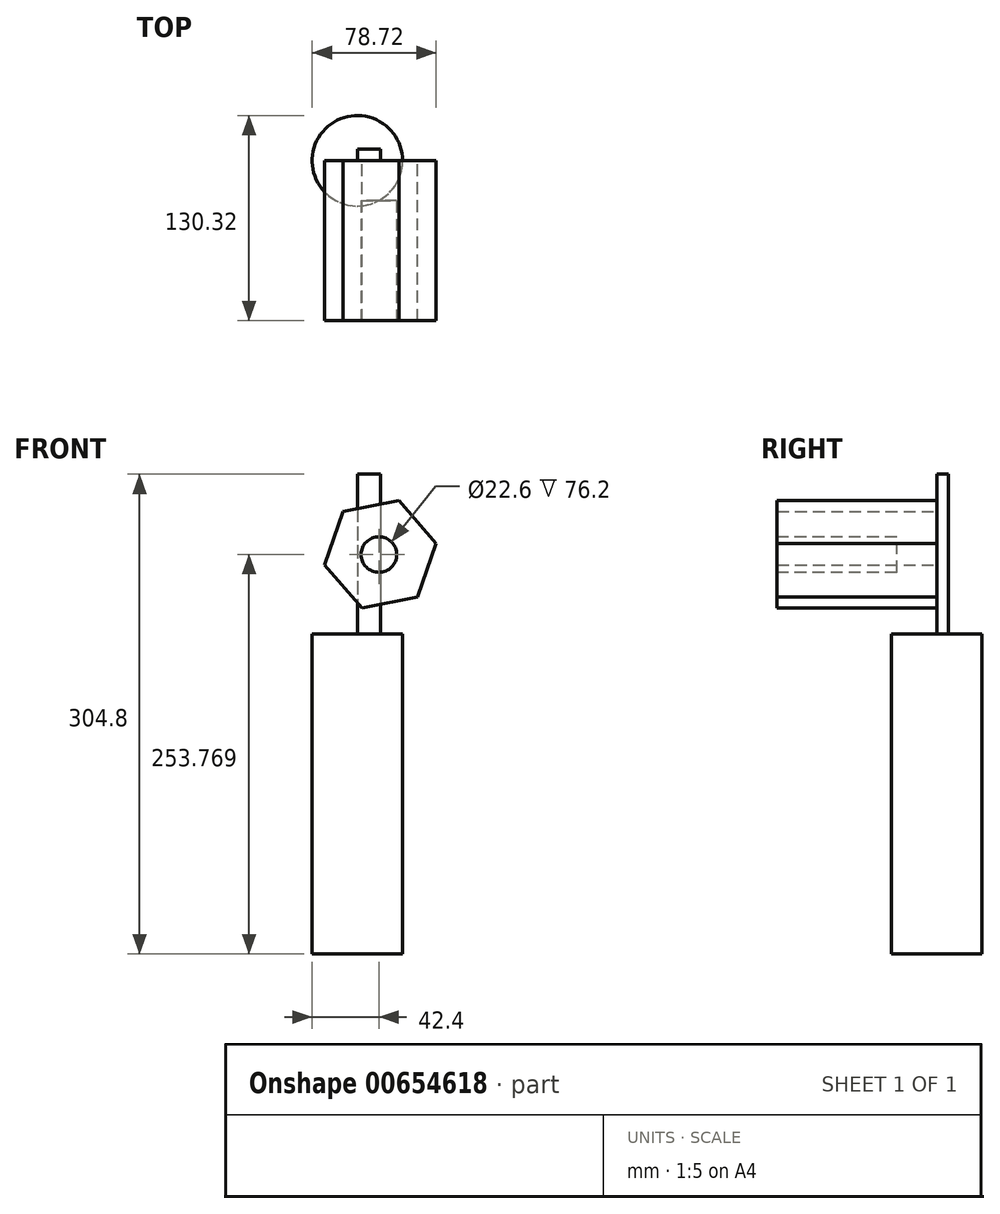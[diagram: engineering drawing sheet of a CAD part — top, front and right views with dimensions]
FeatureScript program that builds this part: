
annotation { "Feature Type Name" : "Feature", "Feature Type Description" : "" }
export const myFeature = defineFeature(function(context is Context, id is Id, definition is map)
    precondition{}
    {
        {
            var Q0;
            Q0=qCreatedBy(makeId("Top.planeOp"),FACE);
            var sketch = newSketch(context, id + "F0", { "sketchPlane" : qUnion([Q0])});
            skCircle(sketch, "E0", {"center": v(0, 0) * mm, "radius": 28.72 * mm});
            skSolve(sketch);
        }
        {
            var Q0;
            Q0 = qSketchRegion(id + "F0", true);
            extrude(context, id + "F1", {"entities" : qUnion([Q0]), "depth" : 203.2 * mm, "offsetDistance" : 25.4 * mm});
        }
        {
            var Q0;
            Q0=makeQuery(id+"F1.opExtrude","CAP_FACE",FACE,{"disambiguationData":[OSD([sQuery(id+"F0.wireOp",EDGE,"E0")])],"isStart":false});
            var sketch = newSketch(context, id + "F2", { "sketchPlane" : qUnion([Q0])});
            skLineSegment(sketch, "E1.bottom", {"start": v(0, 0) * mm, "end": v(14.6, 0) * mm});
            skLineSegment(sketch, "E1.top", {"start": v(0, 7.47) * mm, "end": v(14.6, 7.47) * mm});
            skLineSegment(sketch, "E1.left", {"start": v(0, 0) * mm, "end": v(0, 7.47) * mm});
            skLineSegment(sketch, "E1.right", {"start": v(14.6, 0) * mm, "end": v(14.6, 7.47) * mm});
            skSolve(sketch);
        }
        {
            var Q0;
            Q0 = qSketchRegion(id + "F2", true);
            extrude(context, id + "F3", {"entities" : qUnion([Q0]), "operationType" : NewBodyOperationType.ADD, "depth" : 101.6 * mm, "offsetDistance" : 25.4 * mm});
        }
        {
            var Q0;
            Q0=makeQuery(id+"F3.opExtrude","SWEPT_FACE",FACE,{"disambiguationData":[OSD([sQuery(id+"F2.wireOp",EDGE,"E1.bottom")])]});
            var sketch = newSketch(context, id + "F4", { "sketchPlane" : qUnion([Q0])});
            skCircle(sketch, "E2.cCircle", {"center": v(14.6, 254) * mm, "radius": 31.24 * mm, "construction": true});
            skLineSegment(sketch, "E2.0", {"start": v(50, 260.9) * mm, "end": v(38.27, 226.79) * mm});
            skLineSegment(sketch, "E2.1", {"start": v(38.27, 226.79) * mm, "end": v(2.86, 219.89) * mm});
            skLineSegment(sketch, "E2.2", {"start": v(2.86, 219.89) * mm, "end": v(-20.82, 247.1) * mm});
            skLineSegment(sketch, "E2.3", {"start": v(-20.82, 247.1) * mm, "end": v(-9.09, 281.21) * mm});
            skLineSegment(sketch, "E2.4", {"start": v(-9.09, 281.21) * mm, "end": v(26.32, 288.11) * mm});
            skLineSegment(sketch, "E2.5", {"start": v(26.32, 288.11) * mm, "end": v(50, 260.9) * mm});
            skPoint(sketch, "E2.0.midPoint", {"position": v(44.13, 243.84) * mm});
            skSolve(sketch);
        }
        {
            var Q0;
            Q0 = qSketchRegion(id + "F4", true);
            extrude(context, id + "F5", {"entities" : qUnion([Q0]), "operationType" : NewBodyOperationType.ADD, "depth" : 101.6 * mm, "offsetDistance" : 25.4 * mm});
        }
        {
            var Q0;
            Q0=makeQuery(id+"F5.opExtrude","CAP_FACE",FACE,{"disambiguationData":[OSD([sQuery(id+"F4.wireOp",EDGE,"E2.0"),sQuery(id+"F4.wireOp",EDGE,"E2.1"),sQuery(id+"F4.wireOp",EDGE,"E2.2"),sQuery(id+"F4.wireOp",EDGE,"E2.3"),sQuery(id+"F4.wireOp",EDGE,"E2.4"),sQuery(id+"F4.wireOp",EDGE,"E2.5")])],"isStart":false});
            var sketch = newSketch(context, id + "F6", { "sketchPlane" : qUnion([Q0])});
            skCircle(sketch, "E3", {"center": v(13.68, 253.77) * mm, "radius": 11.3 * mm});
            skSolve(sketch);
        }
        {
            var Q0;
            Q0 = qSketchRegion(id + "F6", true);
            extrude(context, id + "F7", {"entities" : qUnion([Q0]), "operationType" : NewBodyOperationType.REMOVE, "oppositeDirection" : true, "depth" : 76.2 * mm, "offsetDistance" : 25.4 * mm});
        }
    });
